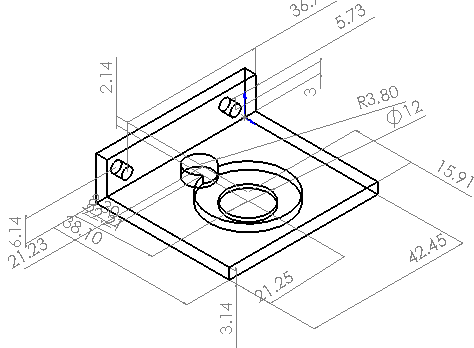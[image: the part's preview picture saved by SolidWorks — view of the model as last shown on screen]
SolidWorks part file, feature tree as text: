
SOLIDWORKS PART (.sldprt)
format: sldprt  version: not decoded by parser v0  size: 246,272 bytes
history: native  units: mm
features: sketch x5, cut_extrude x4, extrude x1 + 1 further entry (+10 scaffold rows collapsed)
feature tree (21):
  "Annotations"  RD1=42.45mm RD2=38.1mm RD3=3.14mm RD4=5.725mm RD5=36.725mm RD6=3mm RD7=6.14mm RD8=15.91mm RD9=21.225mm RD10=2.14mm RD11=22.212521mm RD12=21.248544mm RD13=8.3mm RD14=3.8mm RD15=12mm
  scaffold x10  (default folders/planes/origin — collapsed)
  sketch  "Sketch1"
  extrude  "Extrude1"  Depth=42.45mm
  sketch  "Sketch2"  dims[D1=~1.884375mm]
  cut_extrude  "Cut-Extrude1"  [1 undecoded]
  sketch  "Sketch3"  dims[D1=4.0mm]
  cut_extrude  "Cut-Extrude2"  [1 undecoded]
  sketch  "Sketch4"  dims[D1=~5.723813mm]
  cut_extrude  "Cut-Extrude3"  Depth=2.14mm
  sketch  "Sketch5"
  cut_extrude  "Cut-Extrude4"  [1 undecoded]
decode coverage: 5 of 10 modeling features carry decoded parameters; 1 rows unclassified (native names shown)
note: ~ marks probable driven/reference dimensions
note: 3 parameter values undecoded
summary: no parameter record found for 3 features
note: suppression state not decoded; provenance and decode notes live in map.json
